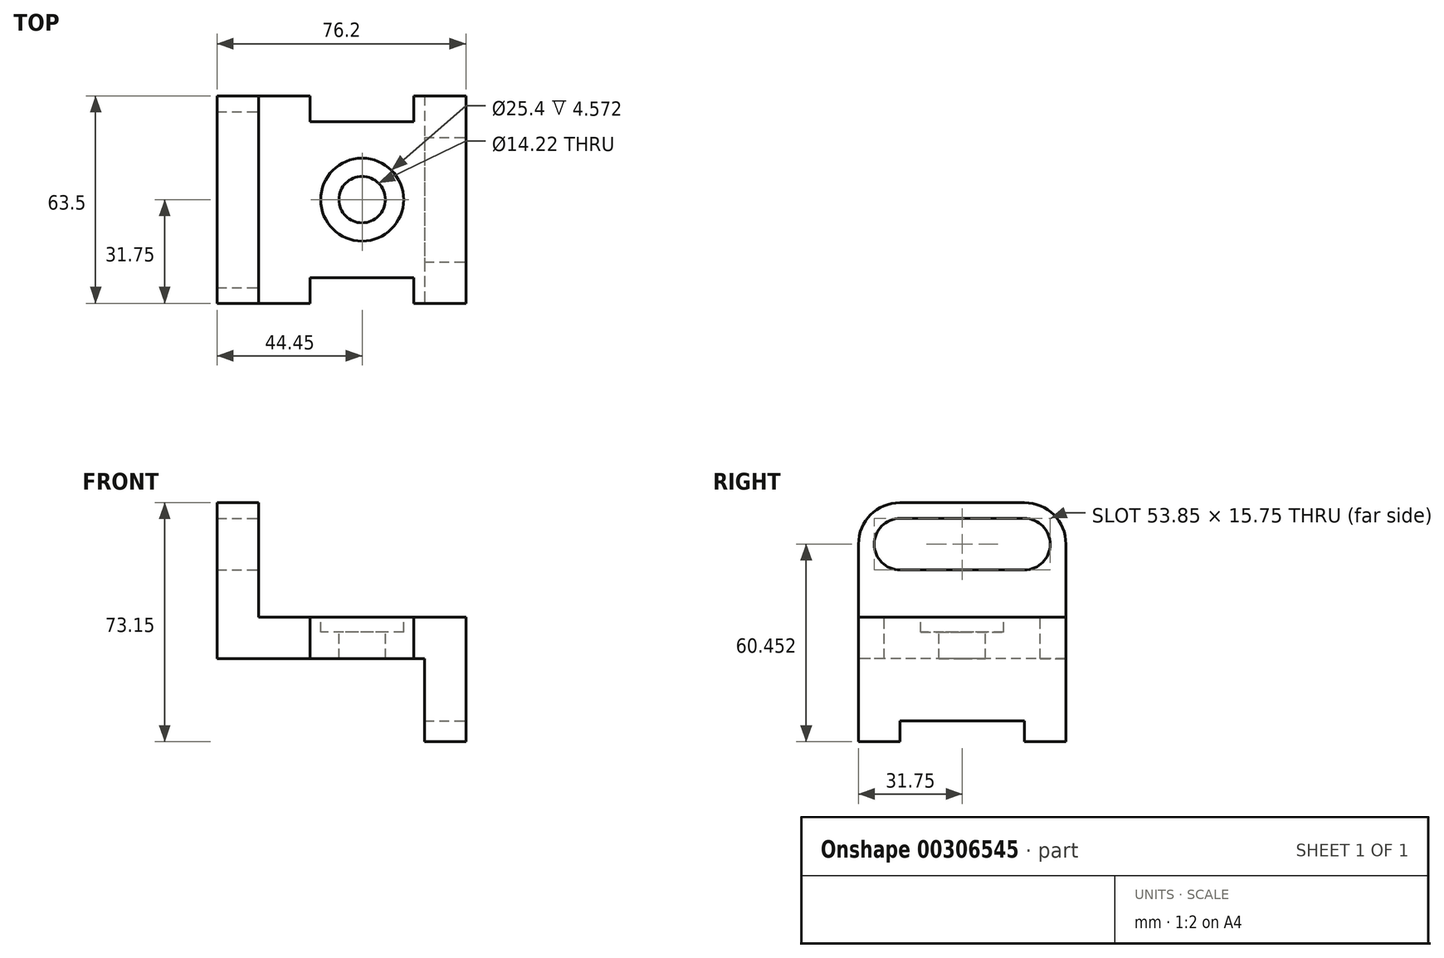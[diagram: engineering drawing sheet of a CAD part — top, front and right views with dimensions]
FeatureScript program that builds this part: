
annotation { "Feature Type Name" : "Feature", "Feature Type Description" : "" }
export const myFeature = defineFeature(function(context is Context, id is Id, definition is map)
    precondition{}
    {
        {
            var Q0;
            Q0=qCreatedBy(makeId("Front.planeOp"),FACE);
            var sketch = newSketch(context, id + "F0", { "sketchPlane" : qUnion([Q0])});
            skLineSegment(sketch, "E0.bottom", {"start": v(0, 0) * mm, "end": v(76.2, 0) * mm});
            skLineSegment(sketch, "E0.top", {"start": v(0, 76.2) * mm, "end": v(76.2, 76.2) * mm});
            skLineSegment(sketch, "E0.left", {"start": v(0, 0) * mm, "end": v(0, 76.2) * mm});
            skLineSegment(sketch, "E0.right", {"start": v(76.2, 0) * mm, "end": v(76.2, 76.2) * mm});
            skSolve(sketch);
        }
        {
            var Q0;
            Q0 = qSketchRegion(id + "F0", true);
            extrude(context, id + "F1", {"entities" : qUnion([Q0]), "endBound" : BoundingType.SYMMETRIC, "oppositeDirection" : true, "depth" : 63.5 * mm});
        }
        {
            var Q0;
            Q0=makeQuery(id+"F1.opExtrude","SWEPT_FACE",FACE,{"disambiguationData":[OSD([sQuery(id+"F0.wireOp",EDGE,"E0.right")])]});
            var sketch = newSketch(context, id + "F2", { "sketchPlane" : qUnion([Q0])});
            skLineSegment(sketch, "E1.top", {"start": v(-31.75, 38.1) * mm, "end": v(31.75, 38.1) * mm});
            skLineSegment(sketch, "E2", {"start": v(-31.75, 38.1) * mm, "end": v(-31.75, 76.2) * mm});
            skLineSegment(sketch, "E3", {"start": v(-31.75, 76.2) * mm, "end": v(31.75, 76.2) * mm});
            skLineSegment(sketch, "E4", {"start": v(31.75, 76.2) * mm, "end": v(31.75, 38.1) * mm});
            skSolve(sketch);
        }
        {
            var Q0;
            Q0 = qSketchRegion(id + "F2", true);
            extrude(context, id + "F3", {"entities" : qUnion([Q0]), "operationType" : NewBodyOperationType.REMOVE, "oppositeDirection" : true, "depth" : 63.5 * mm});
        }
        {
            var Q0;
            Q0=makeQuery(id+"F1.opExtrude","SWEPT_FACE",FACE,{"disambiguationData":[OSD([sQuery(id+"F0.wireOp",EDGE,"E0.right")])]});
            var sketch = newSketch(context, id + "F4", { "sketchPlane" : qUnion([Q0])});
            skLineSegment(sketch, "E5", {"start": v(-31.75, 0) * mm, "end": v(-19.05, 0) * mm});
            skLineSegment(sketch, "E6", {"start": v(31.75, 0) * mm, "end": v(19.05, 0) * mm});
            skLineSegment(sketch, "E7", {"start": v(-19.05, 0) * mm, "end": v(-19.05, 6.35) * mm});
            skLineSegment(sketch, "E8", {"start": v(-19.05, 6.35) * mm, "end": v(19.05, 6.35) * mm});
            skLineSegment(sketch, "E9", {"start": v(19.05, 6.35) * mm, "end": v(19.05, 0) * mm});
            skLineSegment(sketch, "E10", {"start": v(-19.05, 0) * mm, "end": v(19.05, 0) * mm});
            skArc(sketch, "E11", {"start": v(19.05, 68.33) * mm, "mid": v(26.92, 60.45) * mm, "end": v(19.05, 52.58) * mm});
            skArc(sketch, "E12", {"start": v(-19.05, 68.33) * mm, "mid": v(-26.92, 60.45) * mm, "end": v(-19.05, 52.58) * mm});
            skLineSegment(sketch, "E13", {"start": v(-19.05, 68.33) * mm, "end": v(19.05, 68.33) * mm});
            skLineSegment(sketch, "E14", {"start": v(19.05, 52.58) * mm, "end": v(-19.05, 52.58) * mm});
            skLineSegment(sketch, "E15", {"start": v(-19.05, 60.45) * mm, "end": v(-19.05, 64.67) * mm, "construction": true});
            skLineSegment(sketch, "E16", {"start": v(19.05, 60.45) * mm, "end": v(19.05, 65.31) * mm, "construction": true});
            skLineSegment(sketch, "E17", {"start": v(0, 0) * mm, "end": v(0, -8.67) * mm, "construction": true});
            skPoint(sketch, "E17.endSnap0", {"position": v(0, 0) * mm});
            skLineSegment(sketch, "E18", {"start": v(-31.75, 38.1) * mm, "end": v(-31.75, 60.45) * mm});
            skLineSegment(sketch, "E19", {"start": v(-19.05, 73.15) * mm, "end": v(19.05, 73.15) * mm});
            skLineSegment(sketch, "E20", {"start": v(31.75, 38.1) * mm, "end": v(31.75, 60.45) * mm});
            skArc(sketch, "E21", {"start": v(-31.75, 60.45) * mm, "mid": v(-28.03, 69.43) * mm, "end": v(-19.05, 73.15) * mm});
            skArc(sketch, "E22", {"start": v(19.05, 73.15) * mm, "mid": v(28.03, 69.43) * mm, "end": v(31.75, 60.45) * mm});
            skLineSegment(sketch, "E23", {"start": v(-31.75, 60.45) * mm, "end": v(-31.75, 76.2) * mm});
            skLineSegment(sketch, "E24", {"start": v(-31.75, 76.2) * mm, "end": v(31.75, 76.2) * mm});
            skLineSegment(sketch, "E25", {"start": v(31.75, 76.2) * mm, "end": v(31.75, 60.45) * mm});
            skSolve(sketch);
        }
        {
            var Q0;
            Q0 = qSketchRegion(id + "F4", true);
            extrude(context, id + "F5", {"entities" : qUnion([Q0]), "operationType" : NewBodyOperationType.REMOVE, "endBound" : BoundingType.THROUGH_ALL, "oppositeDirection" : true, "depth" : 25.4 * mm});
        }
        {
            var Q0;
            Q0=makeQuery(id+"F3.boolean.opBoolean","COPY",FACE,{"derivedFrom":makeQuery(id+"F3.opExtrude","SWEPT_FACE",FACE,{"disambiguationData":[OSD([sQuery(id+"F2.wireOp",EDGE,"E1.top")])]})});
            var sketch = newSketch(context, id + "F6", { "sketchPlane" : qUnion([Q0])});
            skCircle(sketch, "E26", {"center": v(44.45, 0) * mm, "radius": 12.7 * mm});
            skLineSegment(sketch, "E27", {"start": v(44.45, 0) * mm, "end": v(52.1, 0) * mm, "construction": true});
            skLineSegment(sketch, "E28", {"start": v(44.45, 0) * mm, "end": v(44.45, 6.16) * mm, "construction": true});
            skSolve(sketch);
        }
        {
            var Q0;
            Q0 = qSketchRegion(id + "F6", true);
            extrude(context, id + "F7", {"entities" : qUnion([Q0]), "operationType" : NewBodyOperationType.REMOVE, "oppositeDirection" : true, "depth" : 4.57 * mm});
        }
        {
            var Q0;
            Q0=makeQuery(id+"F7.boolean.opBoolean","COPY",FACE,{"derivedFrom":makeQuery(id+"F7.opExtrude","CAP_FACE",FACE,{"disambiguationData":[OSD([sQuery(id+"F6.wireOp",EDGE,"E26")])],"isStart":false})});
            var sketch = newSketch(context, id + "F8", { "sketchPlane" : qUnion([Q0])});
            skCircle(sketch, "E29", {"center": v(44.45, 0) * mm, "radius": 7.11 * mm});
            skSolve(sketch);
        }
        {
            var Q0;
            Q0 = qSketchRegion(id + "F8", true);
            extrude(context, id + "F9", {"entities" : qUnion([Q0]), "operationType" : NewBodyOperationType.REMOVE, "endBound" : BoundingType.THROUGH_ALL, "oppositeDirection" : true, "depth" : 25.4 * mm});
        }
        {
            var Q0;
            Q0=makeQuery(id+"F3.boolean.opBoolean","COPY",FACE,{"derivedFrom":makeQuery(id+"F3.opExtrude","SWEPT_FACE",FACE,{"disambiguationData":[OSD([sQuery(id+"F2.wireOp",EDGE,"E1.top")])]})});
            var sketch = newSketch(context, id + "F10", { "sketchPlane" : qUnion([Q0])});
            skLineSegment(sketch, "E30", {"start": v(28.45, -31.75) * mm, "end": v(28.45, -23.88) * mm});
            skLineSegment(sketch, "E31", {"start": v(28.45, 31.75) * mm, "end": v(28.45, 23.88) * mm});
            skLineSegment(sketch, "E32", {"start": v(60.2, 31.75) * mm, "end": v(60.2, 23.88) * mm});
            skLineSegment(sketch, "E33", {"start": v(60.2, -31.75) * mm, "end": v(60.2, -23.88) * mm});
            skLineSegment(sketch, "E34", {"start": v(28.45, 23.88) * mm, "end": v(60.2, 23.88) * mm});
            skLineSegment(sketch, "E35", {"start": v(28.45, -23.88) * mm, "end": v(60.2, -23.88) * mm});
            skLineSegment(sketch, "E36", {"start": v(28.45, -31.75) * mm, "end": v(60.2, -31.75) * mm});
            skLineSegment(sketch, "E37", {"start": v(28.45, 31.75) * mm, "end": v(60.2, 31.75) * mm});
            skSolve(sketch);
        }
        {
            var Q0;
            Q0 = qSketchRegion(id + "F10", true);
            extrude(context, id + "F11", {"entities" : qUnion([Q0]), "operationType" : NewBodyOperationType.REMOVE, "endBound" : BoundingType.THROUGH_ALL, "oppositeDirection" : true, "depth" : 25.4 * mm});
        }
        {
            var Q0;
            {var subQ0=sQuery(id+"F0.wireOp",EDGE,"E0.bottom");var subQ1=sQuery(id+"F0.wireOp",EDGE,"E0.right");Q0=makeQuery(id+"F11.boolean.opBoolean","SPLIT",FACE,{"disambiguationData":[TD([makeQuery(id+"F1.opExtrude","SWEPT_FACE",FACE,{"disambiguationData":[OSD([subQ1])]})])],"derivedFrom":makeQuery(id+"F1.opExtrude","CAP_FACE",FACE,{"disambiguationData":[OSD([subQ0,sQuery(id+"F0.wireOp",EDGE,"E0.top"),sQuery(id+"F0.wireOp",EDGE,"E0.left"),subQ1])],"isStart":true})});}
            var sketch = newSketch(context, id + "F12", { "sketchPlane" : qUnion([Q0])});
            skLineSegment(sketch, "E38", {"start": v(63.5, 0) * mm, "end": v(63.5, 25.4) * mm});
            skLineSegment(sketch, "E39", {"start": v(63.5, 25.4) * mm, "end": v(0, 25.4) * mm});
            skLineSegment(sketch, "E40", {"start": v(0, 25.4) * mm, "end": v(0, 0) * mm});
            skLineSegment(sketch, "E41", {"start": v(0, 0) * mm, "end": v(63.5, 0) * mm});
            skSolve(sketch);
        }
        {
            var Q0;
            Q0 = qSketchRegion(id + "F12", true);
            extrude(context, id + "F13", {"entities" : qUnion([Q0]), "operationType" : NewBodyOperationType.REMOVE, "endBound" : BoundingType.THROUGH_ALL, "oppositeDirection" : true, "depth" : 25.4 * mm});
        }
    });
